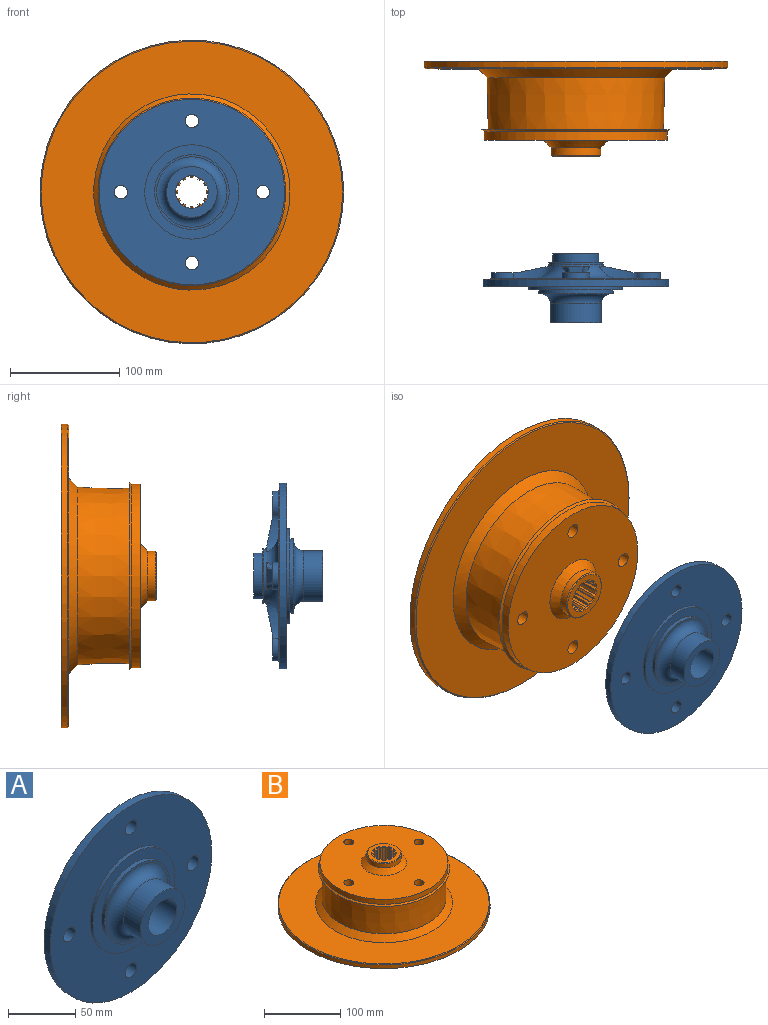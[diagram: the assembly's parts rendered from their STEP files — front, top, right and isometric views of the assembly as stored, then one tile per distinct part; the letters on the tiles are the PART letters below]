
ASSEMBLY  parts=2 mates=1
PART A: 50 faces, bbox 169.9x63x169.9 mm
  f0: torus R=38mm, axis (0,-1,0), area 2595.3mm2, adj f1,f4,f23,f24,f25,f30,f31,f32
  f1: plane 155.85x155.85mm, normal (0,1,0), area 11821.3mm2, adj f0,f5,f22,f23,f24,f29,f30,f31
  f2: cylinder r=21mm len=42mm, axis (0,-1,0), area 1055.6mm2, adj f3,f17
  f3: plane 50x50mm, normal (0,1,0), area 578.1mm2, adj f2,f4
  f4: cylinder r=25mm len=50mm, axis (0,-1,0), area 200.4mm2, adj f0,f3
  f5: cylinder r=77.92mm len=155.85mm, axis (0,-1,0), area 538.6mm2, adj f1,f6
  f6: plane 169.85x169.85mm, normal (0,1,0), area 3581.3mm2, adj f5,f7
  f7: cylinder r=84.92mm len=169.85mm, axis (0,-1,0), area 3468.4mm2, adj f6,f8
  f8: plane 169.85x169.85mm, normal (0,-1,0), area 16340.1mm2, adj f7,f9,f18,f19,f20,f21
  f9: cylinder r=43.12mm len=86.25mm, axis (0,-1,0), area 812.9mm2, adj f8,f10
  f10: plane 86.25x86.25mm, normal (0,-1,0), area 2184.2mm2, adj f9,f11
  f11: cylinder r=34.12mm len=68.25mm, axis (0,-1,0), area 755.6mm2, adj f10,f12
  f12: plane 68.25x68.25mm, normal (0,-1,0), area 401.1mm2, adj f11,f13
  f13: torus R=32.2mm, axis (0,-1,0), area 2351.3mm2, adj f12,f14
  f14: cylinder r=23.2mm len=46.4mm, axis (0,-1,0), area 2565.6mm2, adj f13,f15
  f15: plane 46.4x46.4mm, normal (0,-1,0), area 984.1mm2, adj f14,f16
  f16: cylinder r=15mm len=63mm, axis (0,-1,0), area 5937.6mm2, adj f15,f17
  f17: plane 42x42mm, normal (0,1,0), area 678.6mm2, adj f2,f16
  f18: cylinder r=6.15mm len=12.47mm, axis (0,1,0), area 482mm2, adj f8,f48
  f19: cylinder r=6.15mm len=12.47mm, axis (0,1,0), area 482mm2, adj f8,f41
  f20: cylinder r=6.15mm len=12.47mm, axis (0,1,0), area 482mm2, adj f8,f34
  f21: cylinder r=6.15mm len=12.47mm, axis (0,1,0), area 482mm2, adj f8,f27
  f22: cylinder r=12.5mm len=25mm, axis (0,-1,0), area 273.8mm2, adj f1,f23,f24,f27
  f23: extruded ~35.18x10.9mm, area 246mm2, adj f0,f1,f22,f25,f26,f27,f28
  f24: extruded ~35.18x10.9mm, area 246mm2, adj f0,f1,f22,f25,f26,f27,f28
  f25: cylinder r=25.27mm len=25.01mm, axis (0,-1,0), area 17.4mm2, adj f0,f23,f24,f26
  f26: plane 25.01x3.99mm, normal (0,1,0), area 29.7mm2, adj f23,f24,f25,f28
  f27: plane 25x22.71mm, normal (0,1,0), area 348.8mm2, adj f21,f22,f23,f24,f28
  f28: plane 28.9x18.76mm, normal (0,0.98,0.2), area 392.5mm2, adj f23,f24,f26,f27
  f29: cylinder r=12.5mm len=25mm, axis (0,-1,0), area 273.8mm2, adj f1,f30,f31,f34
  f30: extruded ~35.18x10.9mm, area 246mm2, adj f0,f1,f29,f32,f33,f34,f35
  f31: extruded ~35.18x10.9mm, area 246mm2, adj f0,f1,f29,f32,f33,f34,f35
  f32: cylinder r=25.27mm len=25.01mm, axis (0,-1,0), area 17.4mm2, adj f0,f30,f31,f33
  f33: plane 25.01x3.99mm, normal (0,1,0), area 29.7mm2, adj f30,f31,f32,f35
  f34: plane 25x22.71mm, normal (0,1,0), area 348.8mm2, adj f20,f29,f30,f31,f35
  f35: plane 28.9x18.76mm, normal (0.2,0.98,0), area 392.5mm2, adj f30,f31,f33,f34
  f36: cylinder r=12.5mm len=25mm, axis (0,-1,0), area 273.8mm2, adj f1,f37,f38,f41
  f37: extruded ~35.18x10.9mm, area 246mm2, adj f0,f1,f36,f39,f40,f41,f42
  f38: extruded ~35.18x10.9mm, area 246mm2, adj f0,f1,f36,f39,f40,f41,f42
  f39: cylinder r=25.27mm len=25.01mm, axis (0,-1,0), area 17.7mm2, adj f0,f37,f38,f40
  f40: plane 25.01x3.99mm, normal (0,1,0), area 29.7mm2, adj f37,f38,f39,f42
  f41: plane 25x22.71mm, normal (0,1,0), area 348.8mm2, adj f19,f36,f37,f38,f42
  f42: plane 28.9x18.76mm, normal (0,0.98,-0.2), area 392.5mm2, adj f37,f38,f40,f41
  f43: cylinder r=12.5mm len=25mm, axis (0,-1,0), area 273.8mm2, adj f1,f44,f45,f48
  f44: extruded ~35.18x10.9mm, area 246mm2, adj f0,f1,f43,f46,f47,f48,f49
  f45: extruded ~35.18x10.9mm, area 246mm2, adj f0,f1,f43,f46,f47,f48,f49
  f46: cylinder r=25.27mm len=25.01mm, axis (0,-1,0), area 17.4mm2, adj f0,f44,f45,f47
  f47: plane 25.01x3.99mm, normal (0,1,0), area 29.7mm2, adj f44,f45,f46,f49
  f48: plane 25x22.71mm, normal (0,1,0), area 348.8mm2, adj f18,f43,f44,f45,f49
  f49: plane 28.9x18.76mm, normal (-0.2,0.98,0), area 392.5mm2, adj f44,f45,f47,f48
PART B: 252 faces, bbox 277.8x277.8x87.1 mm
  f0: cylinder r=83.92mm len=167.85mm, axis (0,0,1), area 4123.6mm2, adj f18,f250
  f1: plane 277.82x277.82mm, normal (0,0,-1), area 41823.6mm2, adj f2,f22
  f2: cylinder r=138.91mm len=277.82mm, axis (0,0,1), area 5114.6mm2, adj f1,f251
  f3: cylinder r=14.95mm len=46mm, axis (0,0,1), area 150.8mm2, adj f76,f77,f198,f246
  f4: cylinder r=14.95mm len=46mm, axis (0,0,1), area 150.8mm2, adj f73,f74,f191,f239
  f5: cylinder r=14.95mm len=46mm, axis (0,0,1), area 150.8mm2, adj f70,f71,f183,f231
  f6: cylinder r=14.95mm len=46mm, axis (0,0,1), area 150.8mm2, adj f67,f68,f175,f223
  f7: cylinder r=14.95mm len=46mm, axis (0,0,1), area 150.8mm2, adj f64,f65,f167,f215
  f8: cylinder r=14.95mm len=46mm, axis (0,0,1), area 150.8mm2, adj f61,f62,f159,f207
  f9: cylinder r=14.95mm len=46mm, axis (0,0,1), area 150.8mm2, adj f58,f59,f151,f199
  f10: cylinder r=14.95mm len=46mm, axis (0,0,1), area 150.8mm2, adj f55,f56,f158,f206
  f11: cylinder r=14.95mm len=46mm, axis (0,0,1), area 150.8mm2, adj f52,f53,f166,f214
  f12: cylinder r=14.95mm len=46mm, axis (0,0,1), area 150.8mm2, adj f49,f50,f174,f222
  f13: cylinder r=14.95mm len=46mm, axis (0,0,1), area 150.8mm2, adj f46,f47,f182,f230
  f14: cylinder r=14.95mm len=46mm, axis (0,0,1), area 150.8mm2, adj f44,f79,f190,f238
  f15: plane 40.02x29.02mm, normal (0,0,-1), area 682.3mm2, adj f83,f89,f94,f99,f100,f146
  f16: plane 42.05x29.89mm, normal (0,0,-1), area 740.6mm2, adj f24,f81,f118,f119,f141
  f17: plane 42.05x29.89mm, normal (0,0,-1), area 740.6mm2, adj f24,f82,f120,f125,f136
  f18: plane 167.85x167.85mm, normal (0,0,1), area 18805.8mm2, adj f0,f80,f81,f82,f83,f249
  f19: plane 171.85x171.85mm, normal (0,0,-1), area 3001.3mm2, adj f20,f250
  f20: cone r=81.46mm half-angle=1.3deg, axis (0,0,-1), area 23943.4mm2, adj f19,f248
  f21: plane 275.82x275.82mm, normal (0,0,1), area 34437mm2, adj f248,f251
  f22: cone r=77.41mm half-angle=1.3deg, axis (0,0,-1), area 25056.6mm2, adj f1,f23
  f23: plane 152.3x152.3mm, normal (0,0,-1), area 475.3mm2, adj f22,f126
  f24: cylinder r=73.15mm len=146.3mm, axis (0,0,1), area 2187.8mm2, adj f16,f17,f32,f35,f36,f39,f87,f90
  f25: plane 40.02x29.02mm, normal (0,0,-1), area 682.3mm2, adj f80,f102,f107,f113,f114,f132
  f26: cylinder r=26.66mm len=53.32mm, axis (0,0,1), area 1175.3mm2, adj f84,f93,f108,f122,f128,f129,f130,f131
  f27: plane 51.32x51.32mm, normal (0,0,-1), area 152mm2, adj f127,f128
  f28: cylinder r=22.7mm len=45.4mm, axis (0,0,1), area 727.7mm2, adj f127,f149
  f29: plane 40.57x40.57mm, normal (0,0,-1), area 548.2mm2, adj f150,f151,f152,f153,f154,f155,f156,f157
  f30: plane 43.45x43.45mm, normal (0,0,1), area 738.1mm2, adj f199,f200,f201,f202,f203,f204,f205,f206
  f31: cylinder r=22.72mm len=45.45mm, axis (0,0,1), area 970.9mm2, adj f247,f249
  f32: plane 41.07x9.11mm, normal (-0.98,0.22,0), area 42.1mm2, adj f24,f92,f125,f137
  f33: plane 39.06x8.66mm, normal (0.22,-0.98,0), area 40mm2, adj f96,f101,f102,f131
  f34: plane 59.54x59.54mm, normal (0,0,-1), area 2142.5mm2, adj f92,f93,f95,f96
  f35: plane 41.07x9.11mm, normal (0.98,0.22,0), area 42.1mm2, adj f24,f120,f121,f134
  f36: plane 41.07x9.11mm, normal (-0.22,-0.98,0), area 42.1mm2, adj f24,f119,f124,f142
  f37: plane 59.54x59.54mm, normal (0,0,-1), area 2142.5mm2, adj f121,f122,f123,f124
  f38: plane 39.06x8.66mm, normal (0.98,-0.22,0), area 40mm2, adj f86,f89,f90,f147
  f39: plane 41.07x9.11mm, normal (-0.22,0.98,0), area 42.1mm2, adj f24,f85,f118,f139
  f40: plane 59.54x59.54mm, normal (0,0,-1), area 2142.5mm2, adj f84,f85,f86,f87
  f41: plane 39.06x8.66mm, normal (0.22,0.98,0), area 40mm2, adj f111,f114,f117,f129
  f42: plane 39.06x8.66mm, normal (-0.98,-0.22,0), area 40mm2, adj f99,f105,f106,f144
  f43: plane 59.54x59.54mm, normal (0,0,-1), area 2142.5mm2, adj f105,f108,f111,f112
  f44: plane 46x1.83mm, normal (0.82,0.57,0), area 102.3mm2, adj f14,f45,f188,f236
  f45: plane 46x2mm, normal (0,1,0), area 92mm2, adj f44,f46,f186,f234
  f46: plane 46x1.83mm, normal (-0.82,0.57,0), area 102.3mm2, adj f13,f45,f184,f232
  f47: plane 46x2.22mm, normal (1,0.08,0), area 102.3mm2, adj f13,f48,f180,f228
  f48: plane 46x1.73mm, normal (0.5,0.87,0), area 92mm2, adj f47,f49,f178,f226
  f49: plane 46x2.01mm, normal (-0.43,0.9,0), area 102.3mm2, adj f12,f48,f176,f224
  f50: plane 46x2.01mm, normal (0.9,-0.43,0), area 102.3mm2, adj f12,f51,f172,f220
  f51: plane 46x1.73mm, normal (0.87,0.5,0), area 92mm2, adj f50,f52,f170,f218
  f52: plane 46x2.22mm, normal (0.08,1,0), area 102.3mm2, adj f11,f51,f168,f216
  f53: plane 46x1.83mm, normal (0.57,-0.82,0), area 102.3mm2, adj f11,f54,f164,f212
  f54: plane 46x2mm, normal (1,0,0), area 92mm2, adj f53,f55,f162,f210
  f55: plane 46x1.83mm, normal (0.57,0.82,0), area 102.3mm2, adj f10,f54,f160,f208
  f56: plane 46x2.22mm, normal (0.08,-1,0), area 102.3mm2, adj f10,f57,f156,f204
  f57: plane 46x1.73mm, normal (0.87,-0.5,0), area 92mm2, adj f56,f58,f154,f202
  f58: plane 46x2.01mm, normal (0.9,0.43,0), area 102.3mm2, adj f9,f57,f152,f200
  f59: plane 46x2.01mm, normal (-0.43,-0.9,0), area 102.3mm2, adj f9,f60,f153,f201
  f60: plane 46x1.73mm, normal (0.5,-0.87,0), area 92mm2, adj f59,f61,f155,f203
  f61: plane 46x2.22mm, normal (1,-0.08,0), area 102.3mm2, adj f8,f60,f157,f205
  f62: plane 46x1.83mm, normal (-0.82,-0.57,0), area 102.3mm2, adj f8,f63,f161,f209
  f63: plane 46x2mm, normal (0,-1,0), area 92mm2, adj f62,f64,f163,f211
  f64: plane 46x1.83mm, normal (0.82,-0.57,0), area 102.3mm2, adj f7,f63,f165,f213
  f65: plane 46x2.22mm, normal (-1,-0.08,0), area 102.3mm2, adj f7,f66,f169,f217
  f66: plane 46x1.73mm, normal (-0.5,-0.87,0), area 92mm2, adj f65,f67,f171,f219
  f67: plane 46x2.01mm, normal (0.43,-0.9,0), area 102.3mm2, adj f6,f66,f173,f221
  f68: plane 46x2.01mm, normal (-0.9,0.43,0), area 102.3mm2, adj f6,f69,f177,f225
  f69: plane 46x1.73mm, normal (-0.87,-0.5,0), area 92mm2, adj f68,f70,f179,f227
  f70: plane 46x2.22mm, normal (-0.08,-1,0), area 102.3mm2, adj f5,f69,f181,f229
  f71: plane 46x1.83mm, normal (-0.57,0.82,0), area 102.3mm2, adj f5,f72,f185,f233
  f72: plane 46x2mm, normal (-1,0,0), area 92mm2, adj f71,f73,f187,f235
  f73: plane 46x1.83mm, normal (-0.57,-0.82,0), area 102.3mm2, adj f4,f72,f189,f237
  f74: plane 46x2.22mm, normal (-0.08,1,0), area 102.3mm2, adj f4,f75,f193,f241
  f75: plane 46x1.73mm, normal (-0.87,0.5,0), area 92mm2, adj f74,f76,f195,f243
  f76: plane 46x2.01mm, normal (-0.9,-0.43,0), area 102.3mm2, adj f3,f75,f197,f245
  f77: plane 46x2.01mm, normal (0.43,0.9,0), area 102.3mm2, adj f3,f78,f196,f244
  f78: plane 46x1.73mm, normal (-0.5,0.87,0), area 92mm2, adj f77,f79,f194,f242
  f79: plane 46x2.22mm, normal (-1,0.08,0), area 102.3mm2, adj f14,f78,f192,f240
  f80: cylinder r=6.5mm len=15.23mm, axis (0,0,1), area 622.2mm2, adj f18,f25,f110
  f81: cylinder r=6.5mm len=15.23mm, axis (0,0,1), area 622.2mm2, adj f16,f18
  f82: cylinder r=6.5mm len=15.23mm, axis (0,0,1), area 622.2mm2, adj f17,f18
  f83: cylinder r=6.5mm len=15.23mm, axis (0,0,1), area 622.2mm2, adj f15,f18,f97
  f84: torus R=28.66mm, axis (0,0,-1), area 75.8mm2, adj f26,f40,f85,f86,f139,f147
  f85: cylinder r=2mm len=44.71mm, axis (-0.98,-0.22,0), area 136mm2, adj f39,f40,f84,f87,f139
  f86: cylinder r=2mm len=42.7mm, axis (0.22,0.98,0), area 131.9mm2, adj f38,f40,f84,f88,f147
  f87: torus R=71.15mm, axis (0,0,-1), area 242.5mm2, adj f24,f40,f85,f88
  f88: sphere r=2mm, area 6.5mm2, adj f86,f87,f90
  f89: cylinder r=2mm len=39.56mm, axis (-0.22,-0.98,0), area 124.9mm2, adj f15,f38,f91,f148
  f90: cylinder r=2mm len=2.47mm, axis (0,0,1), area 3.2mm2, adj f24,f38,f88,f91
  f91: bspline ~4.9x4.75mm, area 13.8mm2, adj f24,f89,f90,f94
  f92: cylinder r=2mm len=44.71mm, axis (-0.22,-0.98,0), area 136mm2, adj f32,f34,f93,f95,f137
  f93: torus R=28.66mm, axis (0,0,-1), area 75.8mm2, adj f26,f34,f92,f96,f131,f137
  f94: torus R=71.15mm, axis (0,0,-1), area 39.7mm2, adj f15,f24,f91,f97
  f95: torus R=71.15mm, axis (0,0,-1), area 242.5mm2, adj f24,f34,f92,f98
  f96: cylinder r=2mm len=42.7mm, axis (0.98,0.22,0), area 131.9mm2, adj f33,f34,f93,f98,f131
  f97: bspline ~5.12x2.14mm, area 13.1mm2, adj f24,f83,f94,f100
  f98: sphere r=2mm, area 6.5mm2, adj f95,f96,f101
  f99: cylinder r=2mm len=39.56mm, axis (-0.22,0.98,0), area 124.9mm2, adj f15,f42,f103,f145
  f100: torus R=71.15mm, axis (0,0,-1), area 39.7mm2, adj f15,f24,f97,f103
  f101: cylinder r=2mm len=2.47mm, axis (0,0,1), area 3.2mm2, adj f24,f33,f98,f104
  f102: cylinder r=2mm len=39.56mm, axis (-0.98,-0.22,0), area 124.9mm2, adj f25,f33,f104,f133
  f103: bspline ~4.91x4.68mm, area 13.8mm2, adj f24,f99,f100,f106
  f104: bspline ~4.91x4.68mm, area 13.8mm2, adj f24,f101,f102,f107
  f105: cylinder r=2mm len=42.7mm, axis (0.22,-0.98,0), area 131.9mm2, adj f42,f43,f108,f109,f144
  f106: cylinder r=2mm len=2.47mm, axis (0,0,1), area 3.2mm2, adj f24,f42,f103,f109
  f107: torus R=71.15mm, axis (0,0,-1), area 39.7mm2, adj f24,f25,f104,f110
  f108: torus R=28.66mm, axis (0,0,-1), area 75.8mm2, adj f26,f43,f105,f111,f129,f144
  f109: sphere r=2mm, area 6.8mm2, adj f105,f106,f112
  f110: bspline ~5.12x2.14mm, area 13.1mm2, adj f24,f80,f107,f113
  f111: cylinder r=2mm len=42.7mm, axis (-0.98,0.22,0), area 131.9mm2, adj f41,f43,f108,f115,f129
  f112: torus R=71.15mm, axis (0,0,-1), area 238.3mm2, adj f24,f43,f109,f115
  f113: torus R=71.15mm, axis (0,0,-1), area 39.7mm2, adj f24,f25,f110,f116
  f114: cylinder r=2mm len=39.56mm, axis (0.98,-0.22,0), area 124.9mm2, adj f25,f41,f116,f130
  f115: sphere r=2mm, area 6.5mm2, adj f111,f112,f117
  f116: bspline ~4.9x4.75mm, area 13.8mm2, adj f24,f113,f114,f117
  f117: cylinder r=2mm len=2.47mm, axis (0,0,1), area 3.2mm2, adj f24,f41,f115,f116
  f118: cylinder r=2mm len=41.51mm, axis (0.98,0.22,0), area 131.3mm2, adj f16,f24,f39,f140
  f119: cylinder r=2mm len=41.51mm, axis (-0.98,0.22,0), area 131.3mm2, adj f16,f24,f36,f143
  f120: cylinder r=2mm len=41.51mm, axis (0.22,-0.98,0), area 131.3mm2, adj f17,f24,f35,f135
  f121: cylinder r=2mm len=44.71mm, axis (-0.22,0.98,0), area 136mm2, adj f35,f37,f122,f123,f134
  f122: torus R=28.66mm, axis (0,0,-1), area 75.8mm2, adj f26,f37,f121,f124,f134,f142
  f123: torus R=71.15mm, axis (0,0,-1), area 246.7mm2, adj f24,f37,f121,f124
  f124: cylinder r=2mm len=44.71mm, axis (0.98,-0.22,0), area 136mm2, adj f36,f37,f122,f123,f142
  f125: cylinder r=2mm len=41.51mm, axis (0.22,0.98,0), area 131.3mm2, adj f17,f24,f32,f138
  f126: torus R=75.15mm, axis (0,0,-1), area 1458.2mm2, adj f23,f24
  f127: torus R=24.7mm, axis (0,0,1), area 462.4mm2, adj f27,f28
  f128: torus R=25.66mm, axis (0,0,1), area 259.5mm2, adj f26,f27
  f129: cylinder r=5mm len=5.66mm, axis (0,0,1), area 13.2mm2, adj f26,f41,f108,f111,f130
  f130: bspline ~8.55x6.93mm, area 41.4mm2, adj f26,f114,f129,f132
  f131: cylinder r=5mm len=5.66mm, axis (0,0,1), area 13.2mm2, adj f26,f33,f93,f96,f133
  f132: torus R=31.66mm, axis (0,0,-1), area 84.8mm2, adj f25,f26,f130,f133
  f133: bspline ~8.55x6.93mm, area 41.4mm2, adj f26,f102,f131,f132
  f134: cylinder r=5mm len=5.66mm, axis (0,0,1), area 13.2mm2, adj f26,f35,f121,f122,f135
  f135: bspline ~8.55x6.93mm, area 41.4mm2, adj f26,f120,f134,f136
  f136: torus R=31.66mm, axis (0,0,-1), area 84.8mm2, adj f17,f26,f135,f138
  f137: cylinder r=5mm len=5.66mm, axis (0,0,1), area 13.2mm2, adj f26,f32,f92,f93,f138
  f138: bspline ~8.55x6.93mm, area 41.4mm2, adj f26,f125,f136,f137
  f139: cylinder r=5mm len=5.66mm, axis (0,0,1), area 13.2mm2, adj f26,f39,f84,f85,f140
  f140: bspline ~8.55x6.93mm, area 41.4mm2, adj f26,f118,f139,f141
  f141: torus R=31.66mm, axis (0,0,-1), area 84.8mm2, adj f16,f26,f140,f143
  f142: cylinder r=5mm len=5.66mm, axis (0,0,1), area 13.2mm2, adj f26,f36,f122,f124,f143
  f143: bspline ~8.55x6.93mm, area 41.4mm2, adj f26,f119,f141,f142
  f144: cylinder r=5mm len=5.66mm, axis (0,0,1), area 13.2mm2, adj f26,f42,f105,f108,f145
  f145: bspline ~8.55x6.93mm, area 41.4mm2, adj f26,f99,f144,f146
  f146: torus R=31.66mm, axis (0,0,-1), area 84.8mm2, adj f15,f26,f145,f148
  f147: cylinder r=5mm len=5.66mm, axis (0,0,1), area 13.2mm2, adj f26,f38,f84,f86,f148
  f148: bspline ~8.55x6.93mm, area 41.4mm2, adj f26,f89,f146,f147
  f149: cone r=22.7mm half-angle=45deg, axis (0,0,1), area 331.4mm2, adj f28,f150
  f150: cone r=20.29mm half-angle=67.5deg, axis (0,0,1), area 99.3mm2, adj f29,f149
  f151: cone r=15.95mm half-angle=45deg, axis (0,0,-1), area 5.7mm2, adj f9,f29,f152,f153
  f152: plane 2.15x2.13mm, normal (0.64,0.3,-0.71), area 3.2mm2, adj f29,f58,f151,f154
  f153: plane 2.15x2.13mm, normal (-0.3,-0.64,-0.71), area 3.2mm2, adj f29,f59,f151,f155
  f154: plane 1.78x1.6mm, normal (0.61,-0.35,-0.71), area 2.1mm2, adj f29,f57,f152,f156
  f155: plane 1.78x1.6mm, normal (0.35,-0.61,-0.71), area 2.1mm2, adj f29,f60,f153,f157
  f156: plane 2.92x1.15mm, normal (0.06,-0.7,-0.71), area 3.2mm2, adj f29,f56,f154,f158
  f157: plane 2.92x1.15mm, normal (0.7,-0.06,-0.71), area 3.2mm2, adj f29,f61,f155,f159
  f158: cone r=15.95mm half-angle=45deg, axis (0,0,-1), area 5.7mm2, adj f10,f29,f156,f160
  f159: cone r=15.95mm half-angle=45deg, axis (0,0,-1), area 5.7mm2, adj f8,f29,f157,f161
  f160: plane 2.91x1.81mm, normal (0.4,0.58,-0.71), area 3.2mm2, adj f29,f55,f158,f162
  f161: plane 2.91x1.81mm, normal (-0.58,-0.4,-0.71), area 3.2mm2, adj f29,f62,f159,f163
  f162: plane 2x1mm, normal (0.71,0,-0.71), area 2.1mm2, adj f29,f54,f160,f164
  f163: plane 2x1mm, normal (0,-0.71,-0.71), area 2.1mm2, adj f29,f63,f161,f165
  f164: plane 2.91x1.81mm, normal (0.4,-0.58,-0.71), area 3.2mm2, adj f29,f53,f162,f166
  f165: plane 2.91x1.81mm, normal (0.58,-0.4,-0.71), area 3.2mm2, adj f29,f64,f163,f167
  f166: cone r=15.95mm half-angle=45deg, axis (0,0,-1), area 5.7mm2, adj f11,f29,f164,f168
  f167: cone r=15.95mm half-angle=45deg, axis (0,0,-1), area 5.7mm2, adj f7,f29,f165,f169
  f168: plane 2.92x1.15mm, normal (0.06,0.7,-0.71), area 3.2mm2, adj f29,f52,f166,f170
  f169: plane 2.92x1.15mm, normal (-0.7,-0.06,-0.71), area 3.2mm2, adj f29,f65,f167,f171
  f170: plane 1.78x1.6mm, normal (0.61,0.35,-0.71), area 2.1mm2, adj f29,f51,f168,f172
  f171: plane 1.78x1.6mm, normal (-0.35,-0.61,-0.71), area 2.1mm2, adj f29,f66,f169,f173
  f172: plane 2.15x2.13mm, normal (0.64,-0.3,-0.71), area 3.2mm2, adj f29,f50,f170,f174
  f173: plane 2.15x2.13mm, normal (0.3,-0.64,-0.71), area 3.2mm2, adj f29,f67,f171,f175
  f174: cone r=15.95mm half-angle=45deg, axis (0,0,-1), area 5.7mm2, adj f12,f29,f172,f176
  f175: cone r=15.95mm half-angle=45deg, axis (0,0,-1), area 5.7mm2, adj f6,f29,f173,f177
  f176: plane 2.15x2.13mm, normal (-0.3,0.64,-0.71), area 3.2mm2, adj f29,f49,f174,f178
  f177: plane 2.15x2.13mm, normal (-0.64,0.3,-0.71), area 3.2mm2, adj f29,f68,f175,f179
  f178: plane 1.78x1.6mm, normal (0.35,0.61,-0.71), area 2.1mm2, adj f29,f48,f176,f180
  f179: plane 1.78x1.6mm, normal (-0.61,-0.35,-0.71), area 2.1mm2, adj f29,f69,f177,f181
  f180: plane 2.92x1.15mm, normal (0.7,0.06,-0.71), area 3.2mm2, adj f29,f47,f178,f182
  f181: plane 2.92x1.15mm, normal (-0.06,-0.7,-0.71), area 3.2mm2, adj f29,f70,f179,f183
  f182: cone r=15.95mm half-angle=45deg, axis (0,0,-1), area 5.7mm2, adj f13,f29,f180,f184
  f183: cone r=15.95mm half-angle=45deg, axis (0,0,-1), area 5.7mm2, adj f5,f29,f181,f185
  f184: plane 2.91x1.81mm, normal (-0.58,0.4,-0.71), area 3.2mm2, adj f29,f46,f182,f186
  f185: plane 2.91x1.81mm, normal (-0.4,0.58,-0.71), area 3.2mm2, adj f29,f71,f183,f187
  f186: plane 2x1mm, normal (0,0.71,-0.71), area 2.1mm2, adj f29,f45,f184,f188
  f187: plane 2x1mm, normal (-0.71,0,-0.71), area 2.1mm2, adj f29,f72,f185,f189
  f188: plane 2.91x1.81mm, normal (0.58,0.4,-0.71), area 3.2mm2, adj f29,f44,f186,f190
  f189: plane 2.91x1.81mm, normal (-0.4,-0.58,-0.71), area 3.2mm2, adj f29,f73,f187,f191
  f190: cone r=15.95mm half-angle=45deg, axis (0,0,-1), area 5.7mm2, adj f14,f29,f188,f192
  f191: cone r=15.95mm half-angle=45deg, axis (0,0,-1), area 5.7mm2, adj f4,f29,f189,f193
  f192: plane 2.92x1.15mm, normal (-0.7,0.06,-0.71), area 3.2mm2, adj f29,f79,f190,f194
  f193: plane 2.92x1.15mm, normal (-0.06,0.7,-0.71), area 3.2mm2, adj f29,f74,f191,f195
  f194: plane 1.78x1.6mm, normal (-0.35,0.61,-0.71), area 2.1mm2, adj f29,f78,f192,f196
  f195: plane 1.78x1.6mm, normal (-0.61,0.35,-0.71), area 2.1mm2, adj f29,f75,f193,f197
  f196: plane 2.15x2.13mm, normal (0.3,0.64,-0.71), area 3.2mm2, adj f29,f77,f194,f198
  f197: plane 2.15x2.13mm, normal (-0.64,-0.3,-0.71), area 3.2mm2, adj f29,f76,f195,f198
  f198: cone r=15.95mm half-angle=45deg, axis (0,0,-1), area 5.7mm2, adj f3,f29,f196,f197
  f199: cone r=14.95mm half-angle=45deg, axis (0,0,1), area 5.7mm2, adj f9,f30,f200,f201
  f200: plane 2.15x2.13mm, normal (0.64,0.3,0.71), area 3.2mm2, adj f30,f58,f199,f202
  f201: plane 2.15x2.13mm, normal (-0.3,-0.64,0.71), area 3.2mm2, adj f30,f59,f199,f203
  f202: plane 1.78x1.6mm, normal (0.61,-0.35,0.71), area 2.1mm2, adj f30,f57,f200,f204
  f203: plane 1.78x1.6mm, normal (0.35,-0.61,0.71), area 2.1mm2, adj f30,f60,f201,f205
  f204: plane 2.92x1.15mm, normal (0.06,-0.7,0.71), area 3.2mm2, adj f30,f56,f202,f206
  f205: plane 2.92x1.15mm, normal (0.7,-0.06,0.71), area 3.2mm2, adj f30,f61,f203,f207
  f206: cone r=14.95mm half-angle=45deg, axis (0,0,1), area 5.7mm2, adj f10,f30,f204,f208
  f207: cone r=14.95mm half-angle=45deg, axis (0,0,1), area 5.7mm2, adj f8,f30,f205,f209
  f208: plane 2.91x1.81mm, normal (0.4,0.58,0.71), area 3.2mm2, adj f30,f55,f206,f210
  f209: plane 2.91x1.81mm, normal (-0.58,-0.4,0.71), area 3.2mm2, adj f30,f62,f207,f211
  f210: plane 2x1mm, normal (0.71,0,0.71), area 2.1mm2, adj f30,f54,f208,f212
  f211: plane 2x1mm, normal (0,-0.71,0.71), area 2.1mm2, adj f30,f63,f209,f213
  f212: plane 2.91x1.81mm, normal (0.4,-0.58,0.71), area 3.2mm2, adj f30,f53,f210,f214
  f213: plane 2.91x1.81mm, normal (0.58,-0.4,0.71), area 3.2mm2, adj f30,f64,f211,f215
  f214: cone r=14.95mm half-angle=45deg, axis (0,0,1), area 5.7mm2, adj f11,f30,f212,f216
  f215: cone r=14.95mm half-angle=45deg, axis (0,0,1), area 5.7mm2, adj f7,f30,f213,f217
  f216: plane 2.92x1.15mm, normal (0.06,0.7,0.71), area 3.2mm2, adj f30,f52,f214,f218
  f217: plane 2.92x1.15mm, normal (-0.7,-0.06,0.71), area 3.2mm2, adj f30,f65,f215,f219
  f218: plane 1.78x1.6mm, normal (0.61,0.35,0.71), area 2.1mm2, adj f30,f51,f216,f220
  f219: plane 1.78x1.6mm, normal (-0.35,-0.61,0.71), area 2.1mm2, adj f30,f66,f217,f221
  f220: plane 2.15x2.13mm, normal (0.64,-0.3,0.71), area 3.2mm2, adj f30,f50,f218,f222
  f221: plane 2.15x2.13mm, normal (0.3,-0.64,0.71), area 3.2mm2, adj f30,f67,f219,f223
  f222: cone r=14.95mm half-angle=45deg, axis (0,0,1), area 5.7mm2, adj f12,f30,f220,f224
  f223: cone r=14.95mm half-angle=45deg, axis (0,0,1), area 5.7mm2, adj f6,f30,f221,f225
  f224: plane 2.15x2.13mm, normal (-0.3,0.64,0.71), area 3.2mm2, adj f30,f49,f222,f226
  f225: plane 2.15x2.13mm, normal (-0.64,0.3,0.71), area 3.2mm2, adj f30,f68,f223,f227
  f226: plane 1.78x1.6mm, normal (0.35,0.61,0.71), area 2.1mm2, adj f30,f48,f224,f228
  f227: plane 1.78x1.6mm, normal (-0.61,-0.35,0.71), area 2.1mm2, adj f30,f69,f225,f229
  f228: plane 2.92x1.15mm, normal (0.7,0.06,0.71), area 3.2mm2, adj f30,f47,f226,f230
  f229: plane 2.92x1.15mm, normal (-0.06,-0.7,0.71), area 3.2mm2, adj f30,f70,f227,f231
  f230: cone r=14.95mm half-angle=45deg, axis (0,0,1), area 5.7mm2, adj f13,f30,f228,f232
  f231: cone r=14.95mm half-angle=45deg, axis (0,0,1), area 5.7mm2, adj f5,f30,f229,f233
  f232: plane 2.91x1.81mm, normal (-0.58,0.4,0.71), area 3.2mm2, adj f30,f46,f230,f234
  f233: plane 2.91x1.81mm, normal (-0.4,0.58,0.71), area 3.2mm2, adj f30,f71,f231,f235
  f234: plane 2x1mm, normal (0,0.71,0.71), area 2.1mm2, adj f30,f45,f232,f236
  f235: plane 2x1mm, normal (-0.71,0,0.71), area 2.1mm2, adj f30,f72,f233,f237
  f236: plane 2.91x1.81mm, normal (0.58,0.4,0.71), area 3.2mm2, adj f30,f44,f234,f238
  f237: plane 2.91x1.81mm, normal (-0.4,-0.58,0.71), area 3.2mm2, adj f30,f73,f235,f239
  f238: cone r=14.95mm half-angle=45deg, axis (0,0,1), area 5.7mm2, adj f14,f30,f236,f240
  f239: cone r=14.95mm half-angle=45deg, axis (0,0,1), area 5.7mm2, adj f4,f30,f237,f241
  f240: plane 2.92x1.15mm, normal (-0.7,0.06,0.71), area 3.2mm2, adj f30,f79,f238,f242
  f241: plane 2.92x1.15mm, normal (-0.06,0.7,0.71), area 3.2mm2, adj f30,f74,f239,f243
  f242: plane 1.78x1.6mm, normal (-0.35,0.61,0.71), area 2.1mm2, adj f30,f78,f240,f244
  f243: plane 1.78x1.6mm, normal (-0.61,0.35,0.71), area 2.1mm2, adj f30,f75,f241,f245
  f244: plane 2.15x2.13mm, normal (0.3,0.64,0.71), area 3.2mm2, adj f30,f77,f242,f246
  f245: plane 2.15x2.13mm, normal (-0.64,-0.3,0.71), area 3.2mm2, adj f30,f76,f243,f246
  f246: cone r=14.95mm half-angle=45deg, axis (0,0,1), area 5.7mm2, adj f3,f30,f244,f245
  f247: cone r=21.73mm half-angle=45deg, axis (0,0,-1), area 197.5mm2, adj f30,f31
  f248: cone r=87.77mm half-angle=45.7deg, axis (0,0,-1), area 6384.1mm2, adj f20,f21
  f249: cone r=22.72mm half-angle=45deg, axis (0,0,-1), area 1652.4mm2, adj f18,f31
  f250: cone r=83.92mm half-angle=45deg, axis (0,0,-1), area 1509.2mm2, adj f0,f19
  f251: cone r=137.91mm half-angle=45deg, axis (0,0,-1), area 1229.9mm2, adj f2,f21
PLACE A at identity fixed
PLACE B rot(axis=(0,-0.71,0.71),180deg) t=(0,241.75,0)mm
MATE slider B.f0 <-> A.f0  axis (0,1,0) through (0,200.15,0)mm
